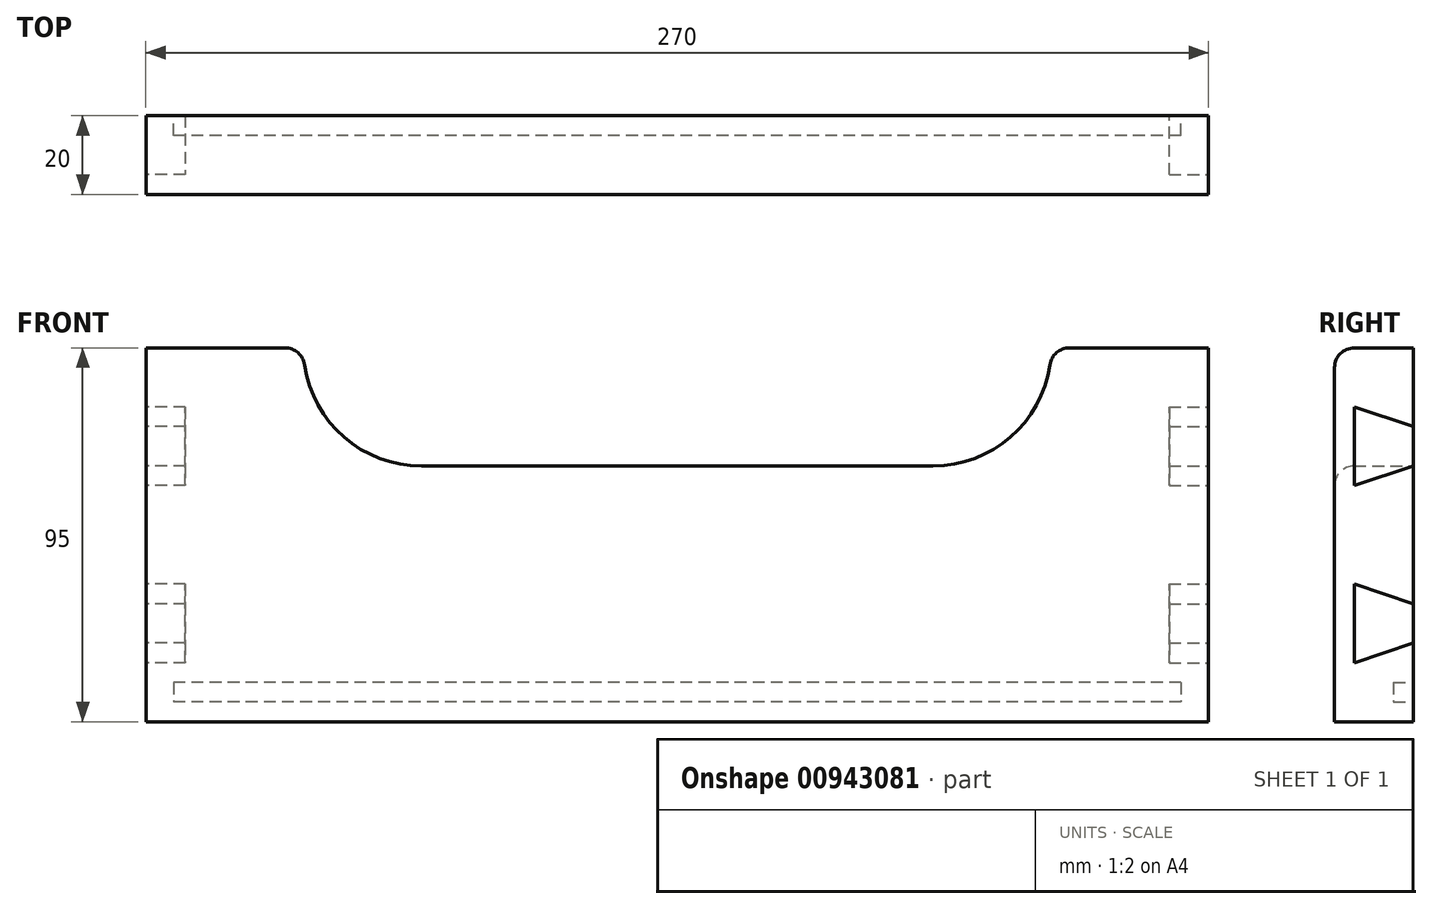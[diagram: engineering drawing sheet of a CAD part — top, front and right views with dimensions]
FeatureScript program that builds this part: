
annotation { "Feature Type Name" : "Feature", "Feature Type Description" : "" }
export const myFeature = defineFeature(function(context is Context, id is Id, definition is map)
    precondition{}
    {
        {
            var Q0;
            Q0=qCreatedBy(makeId("Front.planeOp"),FACE);
            var sketch = newSketch(context, id + "F0", { "sketchPlane" : qUnion([Q0])});
            skLineSegment(sketch, "E0.bottom", {"start": v(-141.95, 33.77) * mm, "end": v(128.05, 33.77) * mm});
            skLineSegment(sketch, "E0.top", {"start": v(-141.95, -61.23) * mm, "end": v(128.05, -61.23) * mm});
            skLineSegment(sketch, "E0.left", {"start": v(-141.95, 33.77) * mm, "end": v(-141.95, -61.23) * mm});
            skLineSegment(sketch, "E0.right", {"start": v(128.05, 33.77) * mm, "end": v(128.05, -61.23) * mm});
            skCircle(sketch, "E1", {"center": v(-71.95, 33.77) * mm, "radius": 30 * mm});
            skCircle(sketch, "E2", {"center": v(58.05, 33.77) * mm, "radius": 30 * mm});
            skLineSegment(sketch, "E3.bottom", {"start": v(-71.95, 33.77) * mm, "end": v(58.05, 33.77) * mm});
            skLineSegment(sketch, "E3.top", {"start": v(-71.95, 3.77) * mm, "end": v(58.05, 3.77) * mm});
            skLineSegment(sketch, "E3.left", {"start": v(-71.95, 33.77) * mm, "end": v(-71.95, 3.77) * mm});
            skLineSegment(sketch, "E3.right", {"start": v(58.05, 33.77) * mm, "end": v(58.05, 3.77) * mm});
            skSolve(sketch);
        }
        {
            var Q0;
            Q0=makeQuery(id+"F0.imprint","IMPRINT",FACE,{"disambiguationData":[TD([[makeQuery(id+"F0.imprint","IMPRINT",EDGE,{"derivedFrom":sQuery(id+"F0.wireOp",EDGE,"E0.top")}),1.0]])]});
            extrude(context, id + "F1", {"entities" : qUnion([Q0]), "depth" : 20 * mm, "offsetDistance" : 25 * mm});
        }
        {
            var Q0;
            Q0=makeQuery(id+"F1.opExtrude","SWEPT_EDGE",EDGE,{"disambiguationData":[OSD([sQuery(id+"F0.wireOp",EDGE,"E0.bottom"),sQuery(id+"F0.wireOp",EDGE,"E1")])]});
            fillet(context, id + "F2", {"entities" : qUnion([Q0]), "radius" : 5 * mm, "tangentPropagation" : true, "allowEdgeOverflow" : false});
        }
        {
            var Q0;
            Q0=makeQuery(id+"F1.opExtrude","SWEPT_EDGE",EDGE,{"disambiguationData":[OSD([sQuery(id+"F0.wireOp",EDGE,"E0.bottom"),sQuery(id+"F0.wireOp",EDGE,"E2")])]});
            fillet(context, id + "F3", {"entities" : qUnion([Q0]), "radius" : 5 * mm, "tangentPropagation" : true, "allowEdgeOverflow" : false});
        }
        {
            var Q0;
            Q0=makeQuery(id+"F1.opExtrude","SWEPT_FACE",FACE,{"disambiguationData":[OSD([sQuery(id+"F0.wireOp",EDGE,"E0.left")])]});
            var sketch = newSketch(context, id + "F4", { "sketchPlane" : qUnion([Q0])});
            skLineSegment(sketch, "E4", {"start": v(0, -41.23) * mm, "end": v(15, -46.23) * mm});
            skLineSegment(sketch, "E5", {"start": v(15, -46.23) * mm, "end": v(15, -26.23) * mm});
            skLineSegment(sketch, "E6", {"start": v(15, -26.23) * mm, "end": v(0, -31.23) * mm});
            skLineSegment(sketch, "E7", {"start": v(0, -31.23) * mm, "end": v(0, 3.77) * mm});
            skLineSegment(sketch, "E8", {"start": v(0, 3.77) * mm, "end": v(15, -1.23) * mm});
            skLineSegment(sketch, "E9", {"start": v(15, -1.23) * mm, "end": v(15, 18.77) * mm});
            skLineSegment(sketch, "E10", {"start": v(15, 18.77) * mm, "end": v(0, 13.77) * mm});
            skSolve(sketch);
        }
        {
            var Q0;
            Q0=makeQuery(id+"F1.opExtrude","CAP_EDGE",EDGE,{"disambiguationData":[OSD([sQuery(id+"F0.wireOp",EDGE,"E3.top")])],"isStart":true});
            cPoint(context, id + "F5", {"entities" : qUnion([Q0]), "parameter" : 0.5});
        }
        {
            var Q0;
            Q0=makeQuery(id+"F1.opExtrude","CAP_EDGE",EDGE,{"disambiguationData":[OSD([sQuery(id+"F0.wireOp",EDGE,"E0.top")])],"isStart":true});
            cPoint(context, id + "F6", {"entities" : qUnion([Q0]), "parameter" : 0.5});
        }
        {
            var Q0;
            Q0=makeQuery(id+"F1.opExtrude","CAP_EDGE",EDGE,{"disambiguationData":[OSD([sQuery(id+"F0.wireOp",EDGE,"E0.top")])],"isStart":false});
            cPoint(context, id + "F7", {"entities" : qUnion([Q0]), "parameter" : 0.5});
        }
        {
            var Q0;
            Q0 = qCreatedBy(id + "F5" ,VERTEX);
            var Q1;
            Q1 = qCreatedBy(id + "F6" ,VERTEX);
            var Q2;
            Q2 = qCreatedBy(id + "F7" ,VERTEX);
            cPlane(context, id + "F8", {"entities" : qUnion([Q0, Q1, Q2]), "cplaneType" : CPlaneType.THREE_POINT, "offset" : 25 * mm, "width" : 150 * mm, "height" : 150 * mm});
        }
        {
            var Q0;
            Q0=makeQuery(id+"F1.opExtrude","CAP_FACE",FACE,{"disambiguationData":[OSD([sQuery(id+"F0.wireOp",EDGE,"E0.bottom"),sQuery(id+"F0.wireOp",EDGE,"E0.top"),sQuery(id+"F0.wireOp",EDGE,"E0.left"),sQuery(id+"F0.wireOp",EDGE,"E0.right"),sQuery(id+"F0.wireOp",EDGE,"E1"),sQuery(id+"F0.wireOp",EDGE,"E2"),sQuery(id+"F0.wireOp",EDGE,"E3.top")])],"isStart":true});
            var sketch = newSketch(context, id + "F9", { "sketchPlane" : qUnion([Q0])});
            skLineSegment(sketch, "E11.bottom", {"start": v(-121.05, -51.23) * mm, "end": v(134.95, -51.23) * mm});
            skLineSegment(sketch, "E11.top", {"start": v(-121.05, -56.23) * mm, "end": v(134.95, -56.23) * mm});
            skLineSegment(sketch, "E11.left", {"start": v(-121.05, -51.23) * mm, "end": v(-121.05, -56.23) * mm});
            skLineSegment(sketch, "E11.right", {"start": v(134.95, -51.23) * mm, "end": v(134.95, -56.23) * mm});
            skSolve(sketch);
        }
        {
            var Q0;
            {var subQ0=sQuery(id+"F4.wireOp",EDGE,"E4");Q0=makeQuery(id+"F4.imprint","IMPRINT",FACE,{"disambiguationData":[TD([[makeQuery(id+"F4.imprint","IMPRINT",EDGE,{"derivedFrom":subQ0}),1.0]])]});}
            var Q1;
            {var subQ0=sQuery(id+"F4.wireOp",EDGE,"E8");Q1=makeQuery(id+"F4.imprint","IMPRINT",FACE,{"disambiguationData":[TD([[makeQuery(id+"F4.imprint","IMPRINT",EDGE,{"derivedFrom":subQ0}),1.0]])]});}
            extrude(context, id + "F10", {"entities" : qUnion([Q0, Q1]), "operationType" : NewBodyOperationType.REMOVE, "oppositeDirection" : true, "depth" : 10 * mm, "offsetDistance" : 25 * mm});
        }
        {
            var Q0;
            Q0=makeQuery(id+"F1.opExtrude","SWEPT_BODY",BODY,{"disambiguationData":[OSD([sQuery(id+"F0.wireOp",EDGE,"E0.bottom"),sQuery(id+"F0.wireOp",EDGE,"E0.top"),sQuery(id+"F0.wireOp",EDGE,"E0.left"),sQuery(id+"F0.wireOp",EDGE,"E0.right"),sQuery(id+"F0.wireOp",EDGE,"E1"),sQuery(id+"F0.wireOp",EDGE,"E2"),sQuery(id+"F0.wireOp",EDGE,"E3.top")])]});
            var Q1;
            Q1=qCreatedBy(id+"F8.planeOp",FACE);
            mirror(context, id + "F11", {"operationType" : NewBodyOperationType.INTERSECT, "entities" : qUnion([Q0]), "mirrorPlane" : qUnion([Q1])});
        }
        {
            var Q0;
            Q0 = qSketchRegion(id + "F9", true);
            extrude(context, id + "F12", {"entities" : qUnion([Q0]), "operationType" : NewBodyOperationType.REMOVE, "oppositeDirection" : true, "depth" : 5 * mm, "offsetDistance" : 25 * mm});
        }
        {
            var Q0;
            Q0=makeQuery(id+"F1.opExtrude","CAP_EDGE",EDGE,{"disambiguationData":[OSD([sQuery(id+"F0.wireOp",EDGE,"E3.top")])],"isStart":false});
            var Q1;
            Q1=makeQuery(id+"F1.opExtrude","CAP_EDGE",EDGE,{"disambiguationData":[OSD([sQuery(id+"F0.wireOp",EDGE,"E1")])],"isStart":false});
            var Q2;
            Q2=makeQuery(id+"F1.opExtrude","CAP_EDGE",EDGE,{"disambiguationData":[OSD([sQuery(id+"F0.wireOp",EDGE,"E2")])],"isStart":false});
            var Q3;
            {var subQ0=sQuery(id+"F0.wireOp",EDGE,"E1");var subQ1=sQuery(id+"F0.wireOp",EDGE,"E0.bottom");Q3=makeQuery(id+"F2.opFillet","BLEND_EDGE",EDGE,{"blendedFrom":[makeQuery(id+"F1.opExtrude","SWEPT_EDGE",EDGE,{"disambiguationData":[OSD([subQ1,subQ0])]}),makeQuery(id+"F1.opExtrude","CAP_FACE",FACE,{"disambiguationData":[OSD([subQ1,sQuery(id+"F0.wireOp",EDGE,"E0.top"),sQuery(id+"F0.wireOp",EDGE,"E0.left"),sQuery(id+"F0.wireOp",EDGE,"E0.right"),subQ0,sQuery(id+"F0.wireOp",EDGE,"E2"),sQuery(id+"F0.wireOp",EDGE,"E3.top")])],"isStart":false})],"blendedInto":[makeQuery(id+"F1.opExtrude","CAP_FACE",FACE,{"disambiguationData":[OSD([subQ1,sQuery(id+"F0.wireOp",EDGE,"E0.top"),sQuery(id+"F0.wireOp",EDGE,"E0.left"),sQuery(id+"F0.wireOp",EDGE,"E0.right"),subQ0,sQuery(id+"F0.wireOp",EDGE,"E2"),sQuery(id+"F0.wireOp",EDGE,"E3.top")])],"isStart":false})]});}
            var Q4;
            {var subQ0=sQuery(id+"F0.wireOp",EDGE,"E2");var subQ1=sQuery(id+"F0.wireOp",EDGE,"E0.bottom");Q4=makeQuery(id+"F3.opFillet","BLEND_EDGE",EDGE,{"blendedFrom":[makeQuery(id+"F1.opExtrude","SWEPT_EDGE",EDGE,{"disambiguationData":[OSD([subQ1,subQ0])]}),makeQuery(id+"F1.opExtrude","CAP_FACE",FACE,{"disambiguationData":[OSD([subQ1,sQuery(id+"F0.wireOp",EDGE,"E0.top"),sQuery(id+"F0.wireOp",EDGE,"E0.left"),sQuery(id+"F0.wireOp",EDGE,"E0.right"),sQuery(id+"F0.wireOp",EDGE,"E1"),subQ0,sQuery(id+"F0.wireOp",EDGE,"E3.top")])],"isStart":false})],"blendedInto":[makeQuery(id+"F1.opExtrude","CAP_FACE",FACE,{"disambiguationData":[OSD([subQ1,sQuery(id+"F0.wireOp",EDGE,"E0.top"),sQuery(id+"F0.wireOp",EDGE,"E0.left"),sQuery(id+"F0.wireOp",EDGE,"E0.right"),sQuery(id+"F0.wireOp",EDGE,"E1"),subQ0,sQuery(id+"F0.wireOp",EDGE,"E3.top")])],"isStart":false})]});}
            var Q5;
            {var subQ0=sQuery(id+"F0.wireOp",EDGE,"E0.bottom");Q5=makeQuery(id+"F1.opExtrude","CAP_EDGE",EDGE,{"disambiguationData":[OSD([subQ0]),TDD([makeQuery(id+"F0.imprint","IMPRINT",EDGE,{"disambiguationData":[TD([[makeQuery(id+"F0.imprint","INTERSECT",VERTEX,{"derivedFrom":[subQ0,sQuery(id+"F0.wireOp",EDGE,"E0.right")]}),1.0]])],"derivedFrom":subQ0})])],"isStart":false});}
            var Q6;
            {var subQ0=sQuery(id+"F0.wireOp",EDGE,"E0.bottom");Q6=makeQuery(id+"F1.opExtrude","CAP_EDGE",EDGE,{"disambiguationData":[OSD([subQ0]),TDD([makeQuery(id+"F0.imprint","IMPRINT",EDGE,{"disambiguationData":[TD([[makeQuery(id+"F0.imprint","INTERSECT",VERTEX,{"derivedFrom":[subQ0,sQuery(id+"F0.wireOp",EDGE,"E0.left")]}),-1.0]])],"derivedFrom":subQ0})])],"isStart":false});}
            fillet(context, id + "F13", {"entities" : qUnion([Q0, Q1, Q2, Q3, Q4, Q5, Q6]), "radius" : 5 * mm, "tangentPropagation" : true, "allowEdgeOverflow" : false});
        }
    });
